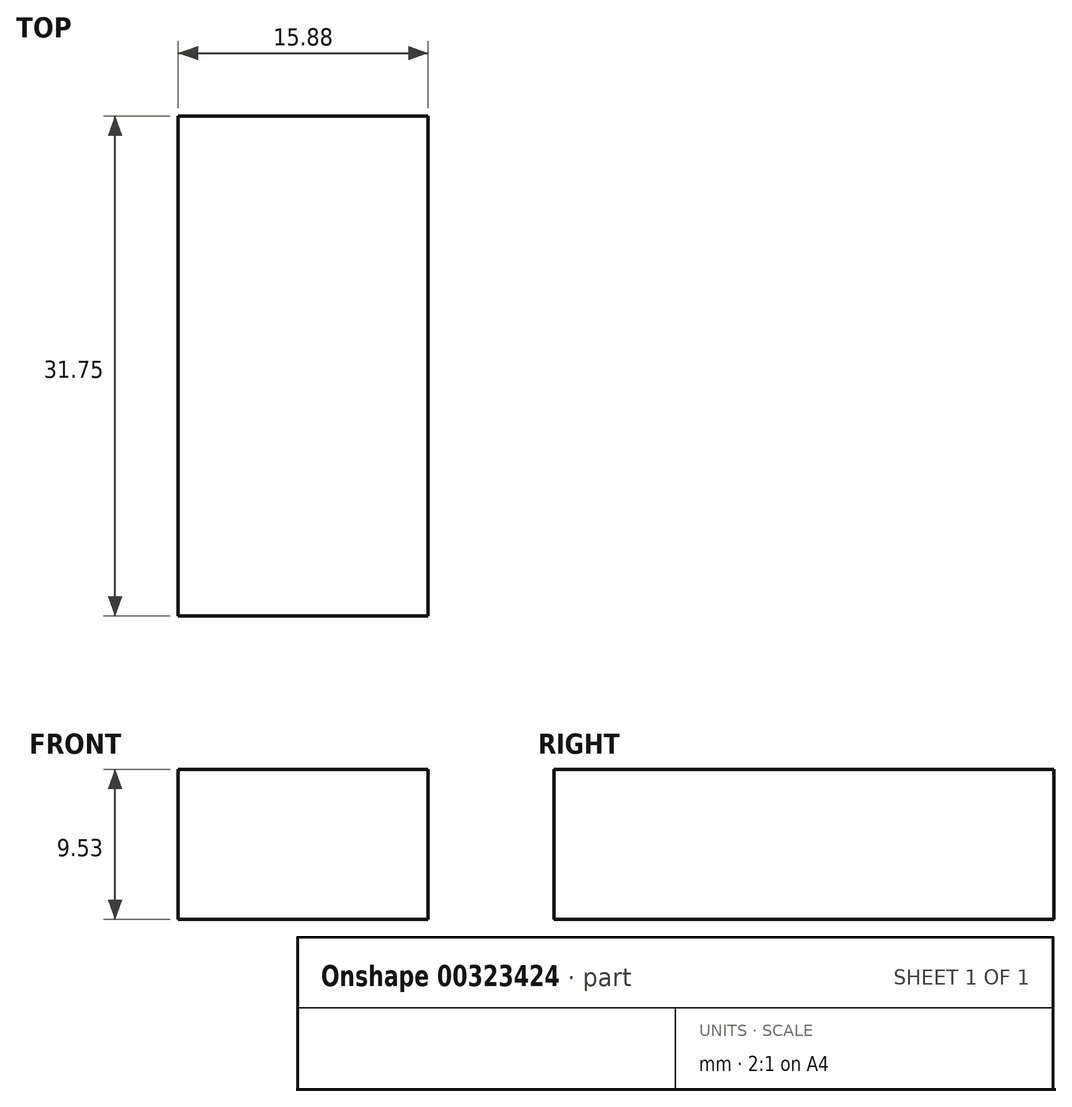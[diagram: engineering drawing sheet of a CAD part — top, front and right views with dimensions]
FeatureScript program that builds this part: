
annotation { "Feature Type Name" : "Feature", "Feature Type Description" : "" }
export const myFeature = defineFeature(function(context is Context, id is Id, definition is map)
    precondition{}
    {
        {
            var Q0;
            Q0=qCreatedBy(makeId("Top.planeOp"),FACE);
            var sketch = newSketch(context, id + "F0", { "sketchPlane" : qUnion([Q0])});
            skLineSegment(sketch, "E0.bottom", {"start": v(0, 0) * mm, "end": v(15.87, 0) * mm});
            skLineSegment(sketch, "E0.top", {"start": v(0, 31.75) * mm, "end": v(15.87, 31.75) * mm});
            skLineSegment(sketch, "E0.left", {"start": v(0, 0) * mm, "end": v(0, 31.75) * mm});
            skLineSegment(sketch, "E0.right", {"start": v(15.87, 0) * mm, "end": v(15.87, 31.75) * mm});
            skSolve(sketch);
        }
        {
            var Q0;
            Q0=makeQuery(id+"F0.imprint","IMPRINT",FACE,{"disambiguationData":[TD([[makeQuery(id+"F0.imprint","IMPRINT",EDGE,{"derivedFrom":sQuery(id+"F0.wireOp",EDGE,"E0.bottom")}),1.0]])]});
            extrude(context, id + "F1", {"entities" : qUnion([Q0]), "depth" : 9.52 * mm});
        }
    });
